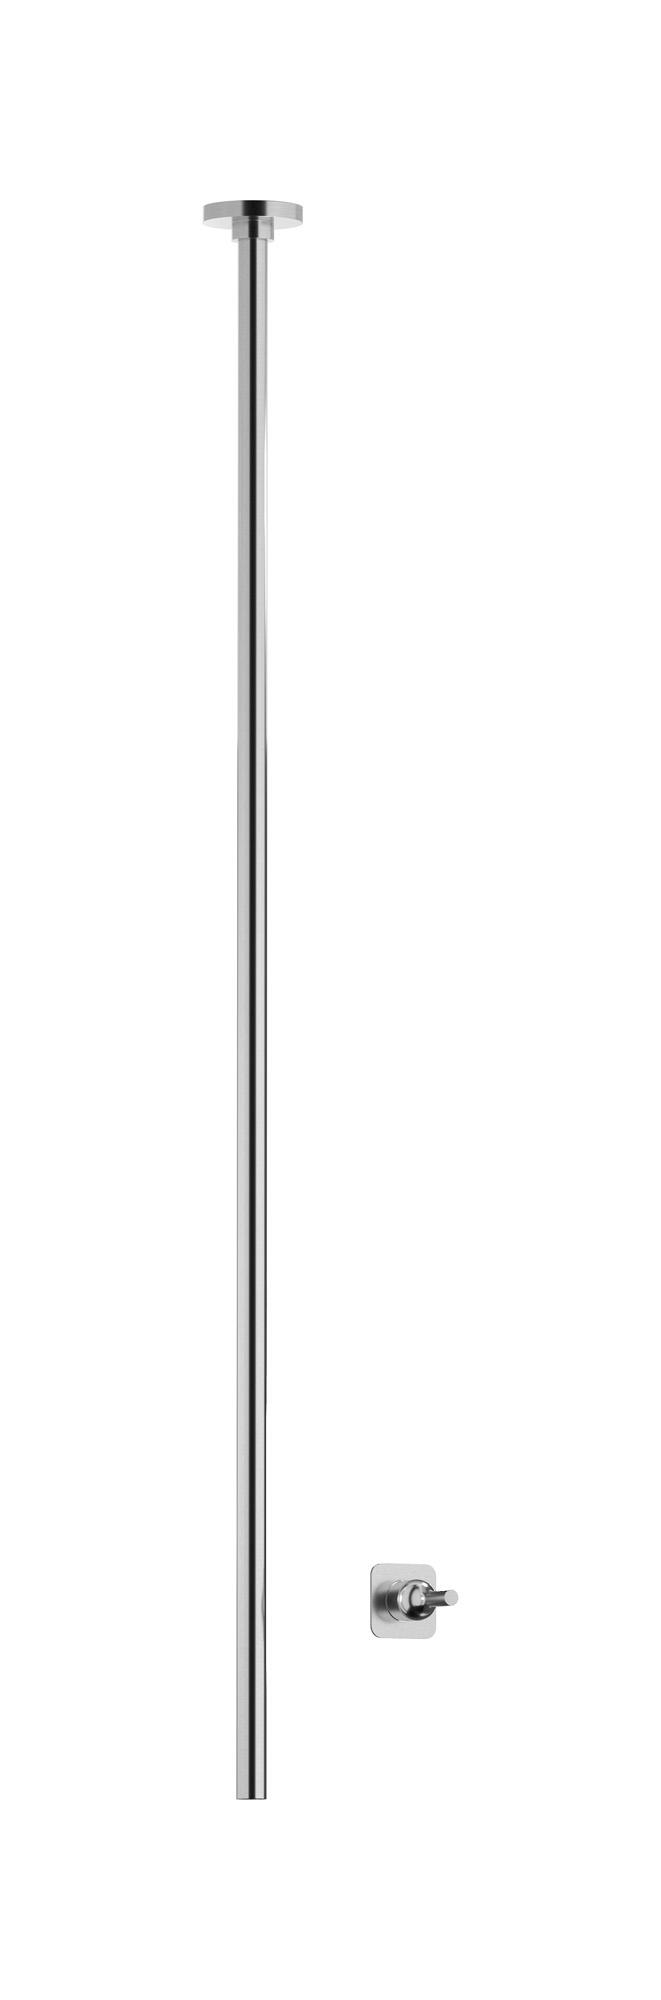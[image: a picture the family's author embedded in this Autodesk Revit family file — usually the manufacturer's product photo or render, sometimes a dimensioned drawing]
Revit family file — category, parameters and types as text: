
# Revit family: BI210
name_source: partatom
category: Apparecchi idraulici
units: mm (PartAtom-declared; Revit-internal decimal feet)

## family parameters
Basato su piano di lavoro = No
Condiviso = No
Mantieni orientamento annotazione = No
Numero OmniClass = 23.45.55.17
Punto di calcolo locali = No
Quota connettore circolare = Usa diametro
Sempre verticale = Sì
Taglio con vuoti quando caricato = No
Tipo di parte = Normale
Titolo OmniClass = Mixing Faucets

## types (4) — shared parameters
Cold water inlet = 10 mm  [stored 0.0328084 ft]
Commenti sul tipo = Wall mixer
Connessione CW = No
Connessione HW = No
Connessione di scarico = No
Connessione di ventilazione = No
Descrizione = Ceiling spout with wall mounted mixer
Hot water inlet = 10 mm  [stored 0.0328084 ft]
Produttore = IB Rubinetterie S.p.A.
URL = https://www.weareib.it
zero-valued in all types: Prospetto di default

## per-type parameters (varying)
| type | Finishes surface | Immagine tipo | Modello |
| Chrome | IB_Chrome | BI210CC.jpg | BI210CC |
| Matt black | IB_matt black | BI210NP.jpg | BI210NP |
| Matt white | IB_matt white | BI210BO.jpg | BI210BO |
| Brushed nickel | IB_Brushed nickel | BI210SS.jpg | BI210SS |

note: [stored X ft] marks values corroborated as IEEE doubles in the binary element streams (Revit-internal decimal feet)
